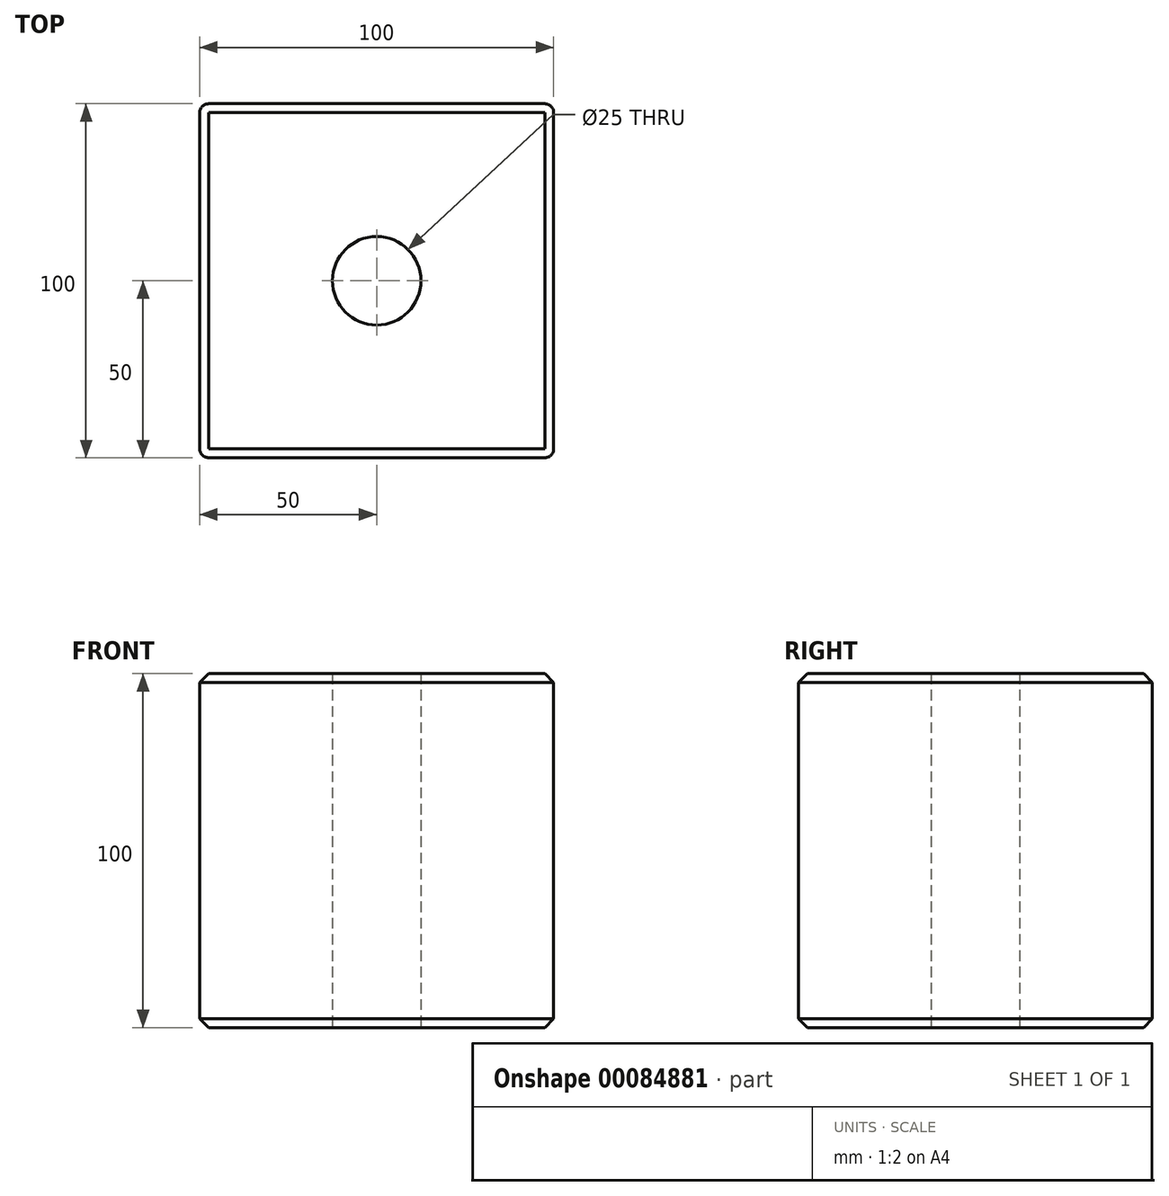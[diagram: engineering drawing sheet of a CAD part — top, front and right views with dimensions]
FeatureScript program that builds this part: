
annotation { "Feature Type Name" : "Feature", "Feature Type Description" : "" }
export const myFeature = defineFeature(function(context is Context, id is Id, definition is map)
    precondition{}
    {
        {
            var Q0;
            Q0=qCreatedBy(makeId("Top.planeOp"),FACE);
            var sketch = newSketch(context, id + "F0", { "sketchPlane" : qUnion([Q0])});
            skLineSegment(sketch, "E0.bottom", {"start": v(-47.5, -50) * mm, "end": v(47.5, -50) * mm});
            skLineSegment(sketch, "E0.top", {"start": v(-47.5, 50) * mm, "end": v(47.5, 50) * mm});
            skLineSegment(sketch, "E0.left", {"start": v(-50, -47.5) * mm, "end": v(-50, 47.5) * mm});
            skLineSegment(sketch, "E0.right", {"start": v(50, -47.5) * mm, "end": v(50, 47.5) * mm});
            skPoint(sketch, "E0.middle", {"position": v(0, 0) * mm});
            skCircle(sketch, "E1", {"center": v(0, 0) * mm, "radius": 12.5 * mm});
            skPoint(sketch, "E2.visualSharp", {"position": v(-50, 50) * mm});
            skArc(sketch, "E2.filletArc", {"start": v(-47.5, 50) * mm, "mid": v(-49.27, 49.27) * mm, "end": v(-50, 47.5) * mm});
            skPoint(sketch, "E3.visualSharp", {"position": v(50, -50) * mm});
            skArc(sketch, "E3.filletArc", {"start": v(47.5, -50) * mm, "mid": v(49.27, -49.27) * mm, "end": v(50, -47.5) * mm});
            skPoint(sketch, "E4.visualSharp", {"position": v(50, 50) * mm});
            skArc(sketch, "E4.filletArc", {"start": v(50, 47.5) * mm, "mid": v(49.27, 49.27) * mm, "end": v(47.5, 50) * mm});
            skPoint(sketch, "E5.visualSharp", {"position": v(-50, -50) * mm});
            skArc(sketch, "E5.filletArc", {"start": v(-50, -47.5) * mm, "mid": v(-49.27, -49.27) * mm, "end": v(-47.5, -50) * mm});
            skSolve(sketch);
        }
        {
            var Q0;
            Q0 = qSketchRegion(id + "F0", true);
            extrude(context, id + "F1", {"entities" : qUnion([Q0]), "endBound" : BoundingType.SYMMETRIC, "depth" : 100 * mm});
        }
        {
            var Q0;
            Q0=makeQuery(id+"F1.opExtrude","CAP_EDGE",EDGE,{"disambiguationData":[OSD([sQuery(id+"F0.wireOp",EDGE,"E0.right")])],"isStart":false});
            var Q1;
            Q1=makeQuery(id+"F1.opExtrude","CAP_EDGE",EDGE,{"disambiguationData":[OSD([sQuery(id+"F0.wireOp",EDGE,"E0.bottom")])],"isStart":false});
            var Q2;
            Q2=makeQuery(id+"F1.opExtrude","CAP_EDGE",EDGE,{"disambiguationData":[OSD([sQuery(id+"F0.wireOp",EDGE,"E0.left")])],"isStart":false});
            var Q3;
            Q3=makeQuery(id+"F1.opExtrude","CAP_EDGE",EDGE,{"disambiguationData":[OSD([sQuery(id+"F0.wireOp",EDGE,"E0.top")])],"isStart":false});
            var Q4;
            Q4=makeQuery(id+"F1.opExtrude","CAP_EDGE",EDGE,{"disambiguationData":[OSD([sQuery(id+"F0.wireOp",EDGE,"E0.right")])],"isStart":true});
            var Q5;
            Q5=makeQuery(id+"F1.opExtrude","CAP_EDGE",EDGE,{"disambiguationData":[OSD([sQuery(id+"F0.wireOp",EDGE,"E0.top")])],"isStart":true});
            chamfer(context, id + "F2", {"entities" : qUnion([Q0, Q1, Q2, Q3, Q4, Q5]), "width" : 2.5 * mm, "tangentPropagation" : true});
        }
    });
